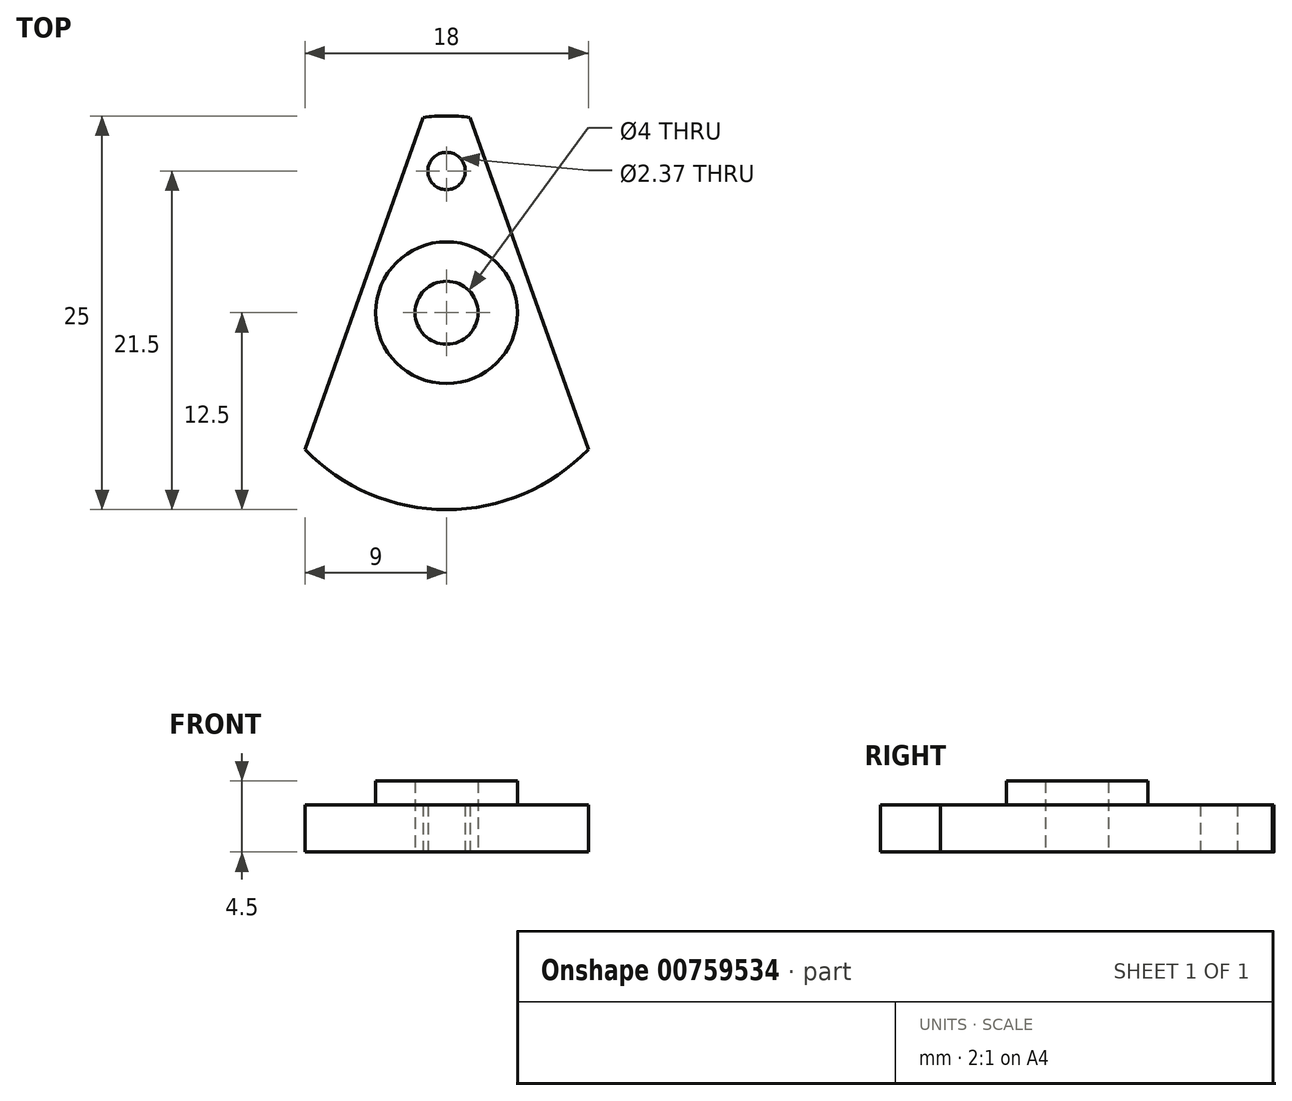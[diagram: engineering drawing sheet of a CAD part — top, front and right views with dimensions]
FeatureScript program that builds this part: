
annotation { "Feature Type Name" : "Feature", "Feature Type Description" : "" }
export const myFeature = defineFeature(function(context is Context, id is Id, definition is map)
    precondition{}
    {
        {
            var Q0;
            Q0=qCreatedBy(makeId("Top.planeOp"),FACE);
            var sketch = newSketch(context, id + "F0", { "sketchPlane" : qUnion([Q0])});
            skArc(sketch, "E0", {"start": v(-9, -8.67) * mm, "mid": v(0, -12.5) * mm, "end": v(9, -8.67) * mm});
            skLineSegment(sketch, "E1", {"start": v(1.5, 12.4) * mm, "end": v(9, -8.67) * mm});
            skLineSegment(sketch, "E2.MirrorCS", {"start": v(-1.5, 12.4) * mm, "end": v(-9, -8.67) * mm});
            skArc(sketch, "E3.trimOffspring", {"start": v(1.5, 12.4) * mm, "mid": v(0, 12.5) * mm, "end": v(-1.5, 12.4) * mm});
            skCircle(sketch, "E4", {"center": v(0, 0) * mm, "radius": 2 * mm});
            skCircle(sketch, "E5", {"center": v(0, 0) * mm, "radius": 4.5 * mm});
            skSolve(sketch);
        }
        {
            var Q0;
            Q0=qCreatedBy(makeId("Top.planeOp"),FACE);
            var sketch = newSketch(context, id + "F1", { "sketchPlane" : qUnion([Q0])});
            skCircle(sketch, "E6", {"center": v(0, 9) * mm, "radius": 1.19 * mm});
            skSolve(sketch);
        }
        {
            var Q0;
            Q0=makeQuery(id+"F0.imprint","IMPRINT",FACE,{"disambiguationData":[TD([[makeQuery(id+"F0.imprint","IMPRINT",EDGE,{"derivedFrom":sQuery(id+"F0.wireOp",EDGE,"E0")}),1.0]])]});
            var Q1;
            Q1=makeQuery(id+"F0.imprint","IMPRINT",FACE,{"disambiguationData":[TD([[makeQuery(id+"F0.imprint","IMPRINT",EDGE,{"derivedFrom":sQuery(id+"F0.wireOp",EDGE,"E4")}),-1.0]])]});
            extrude(context, id + "F2", {"entities" : qUnion([Q0, Q1]), "depth" : 3 * mm, "offsetDistance" : 25 * mm});
        }
        {
            var Q0;
            Q0 = qSketchRegion(id + "F1", true);
            extrude(context, id + "F3", {"entities" : qUnion([Q0]), "operationType" : NewBodyOperationType.REMOVE, "depth" : 25 * mm, "offsetDistance" : 25 * mm});
        }
        {
            var Q0;
            Q0=makeQuery(id+"F0.imprint","IMPRINT",FACE,{"disambiguationData":[TD([[makeQuery(id+"F0.imprint","IMPRINT",EDGE,{"derivedFrom":sQuery(id+"F0.wireOp",EDGE,"E4")}),-1.0]])]});
            extrude(context, id + "F4", {"entities" : qUnion([Q0]), "operationType" : NewBodyOperationType.ADD, "depth" : 4.5 * mm, "offsetDistance" : 25 * mm});
        }
    });
